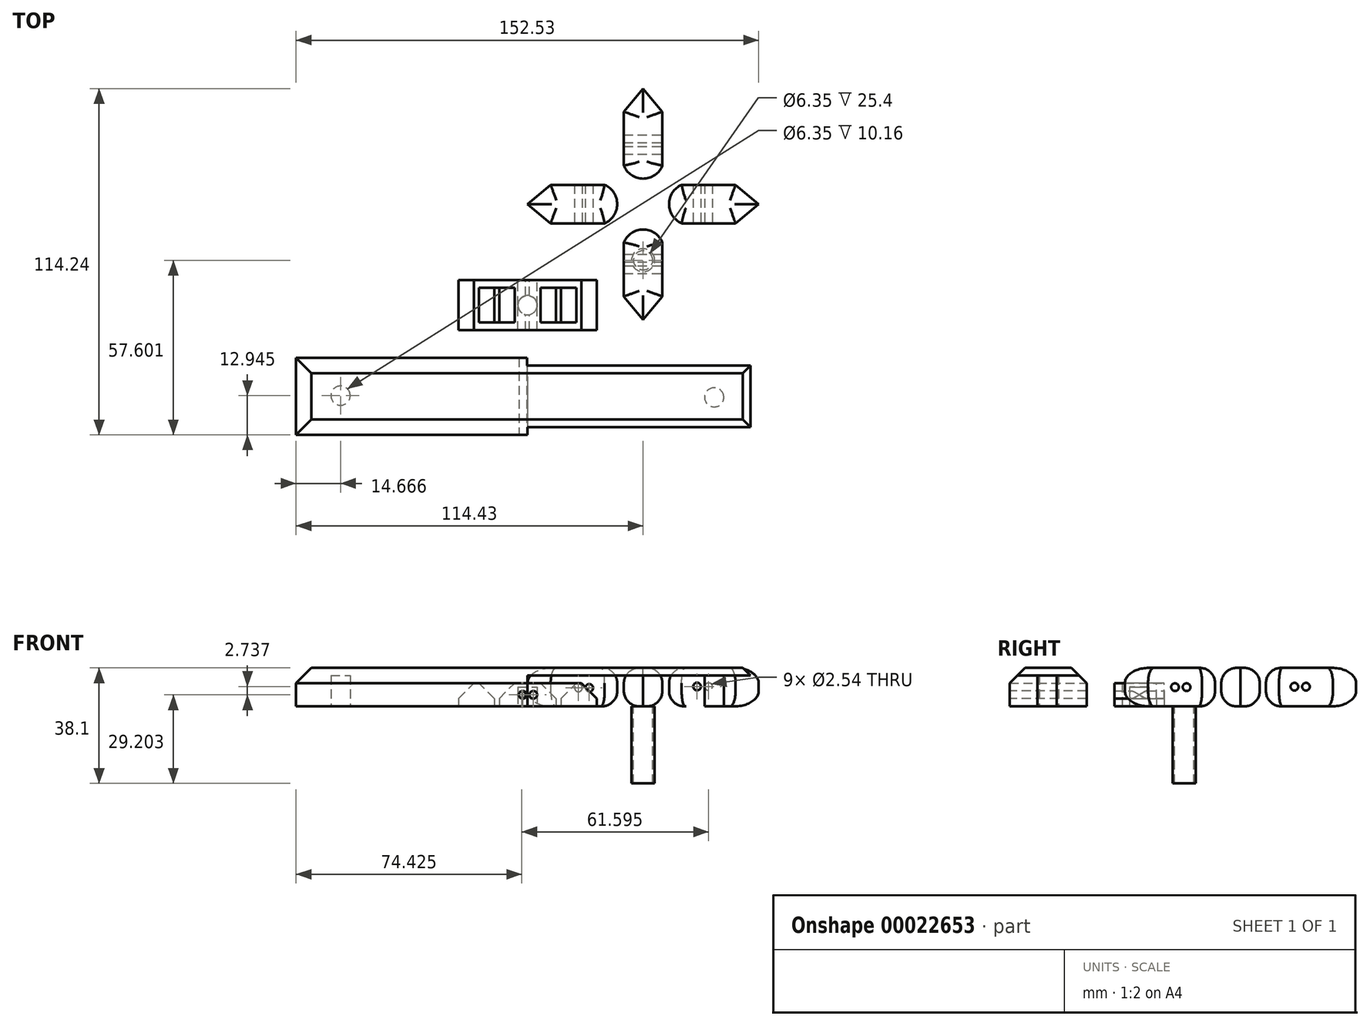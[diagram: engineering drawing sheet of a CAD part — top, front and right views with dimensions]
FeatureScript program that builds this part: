
annotation { "Feature Type Name" : "Feature", "Feature Type Description" : "" }
export const myFeature = defineFeature(function(context is Context, id is Id, definition is map)
    precondition{}
    {
        {
            var Q0;
            Q0=qCreatedBy(makeId("Top.planeOp"),FACE);
            var sketch = newSketch(context, id + "F0", { "sketchPlane" : qUnion([Q0])});
            skLineSegment(sketch, "E0.rect.bottom", {"start": v(76.2, 50.8) * mm, "end": v(-76.2, 50.8) * mm});
            skLineSegment(sketch, "E0.rect.top", {"start": v(76.2, -50.8) * mm, "end": v(-76.2, -50.8) * mm});
            skLineSegment(sketch, "E0.rect.left", {"start": v(76.2, 50.8) * mm, "end": v(76.2, -50.8) * mm});
            skLineSegment(sketch, "E0.rect.right", {"start": v(-76.2, 50.8) * mm, "end": v(-76.2, -50.8) * mm});
            skPoint(sketch, "E0.rect.middle", {"position": v(0, 0) * mm});
            skLineSegment(sketch, "E1", {"start": v(0, 0) * mm, "end": v(76.2, 0) * mm});
            skLineSegment(sketch, "E2", {"start": v(0, 0) * mm, "end": v(-76.2, 0) * mm});
            skLineSegment(sketch, "E3", {"start": v(-76.2, 0) * mm, "end": v(0, 0) * mm});
            skLineSegment(sketch, "E4", {"start": v(38.1, 0) * mm, "end": v(38.1, 12.7) * mm});
            skLineSegment(sketch, "E5", {"start": v(38.1, 0) * mm, "end": v(38.1, -12.7) * mm});
            skLineSegment(sketch, "E6", {"start": v(38.1, 12.7) * mm, "end": v(44.45, 12.7) * mm});
            skLineSegment(sketch, "E7", {"start": v(38.1, 12.7) * mm, "end": v(31.75, 12.7) * mm});
            skLineSegment(sketch, "E8.MirrorCS", {"start": v(38.1, -12.7) * mm, "end": v(44.45, -12.7) * mm});
            skLineSegment(sketch, "E9.MirrorCS", {"start": v(38.1, -12.7) * mm, "end": v(31.75, -12.7) * mm});
            skArc(sketch, "E10", {"start": v(31.75, 12.7) * mm, "mid": v(38.1, 8.38) * mm, "end": v(44.45, 12.7) * mm});
            skLineSegment(sketch, "E11.bottom", {"start": v(31.75, 12.7) * mm, "end": v(44.45, 12.7) * mm});
            skLineSegment(sketch, "E11.top", {"start": v(31.75, 30.48) * mm, "end": v(44.45, 30.48) * mm});
            skLineSegment(sketch, "E11.left", {"start": v(31.75, 12.7) * mm, "end": v(31.75, 30.48) * mm});
            skLineSegment(sketch, "E11.right", {"start": v(44.45, 12.7) * mm, "end": v(44.45, 30.48) * mm});
            skLineSegment(sketch, "E12", {"start": v(38.1, 12.7) * mm, "end": v(38.1, 38.1) * mm});
            skLineSegment(sketch, "E13", {"start": v(31.75, 30.48) * mm, "end": v(38.1, 38.1) * mm});
            skLineSegment(sketch, "E14", {"start": v(38.1, 38.1) * mm, "end": v(44.45, 30.48) * mm});
            skArc(sketch, "E15.MirrorCS", {"start": v(31.75, -12.7) * mm, "mid": v(38.1, -8.38) * mm, "end": v(44.45, -12.7) * mm});
            skLineSegment(sketch, "E16.MirrorCS", {"start": v(38.1, -12.7) * mm, "end": v(38.1, -38.1) * mm});
            skLineSegment(sketch, "E17.MirrorCS", {"start": v(44.45, -12.7) * mm, "end": v(44.45, -30.48) * mm});
            skLineSegment(sketch, "E18.MirrorCS", {"start": v(31.75, -12.7) * mm, "end": v(31.75, -30.48) * mm});
            skLineSegment(sketch, "E19.MirrorCS", {"start": v(31.75, -30.48) * mm, "end": v(44.45, -30.48) * mm});
            skLineSegment(sketch, "E20.MirrorCS", {"start": v(31.75, -30.48) * mm, "end": v(38.1, -38.1) * mm});
            skLineSegment(sketch, "E21.MirrorCS", {"start": v(38.1, -38.1) * mm, "end": v(44.45, -30.48) * mm});
            skLineSegment(sketch, "E22", {"start": v(25.4, 0) * mm, "end": v(25.4, 6.35) * mm});
            skLineSegment(sketch, "E23", {"start": v(25.4, 0) * mm, "end": v(25.4, -6.35) * mm});
            skLineSegment(sketch, "E24.bottom", {"start": v(25.4, 6.35) * mm, "end": v(7.62, 6.35) * mm});
            skLineSegment(sketch, "E24.top", {"start": v(25.4, -6.35) * mm, "end": v(7.62, -6.35) * mm});
            skLineSegment(sketch, "E24.left", {"start": v(25.4, 6.35) * mm, "end": v(25.4, -6.35) * mm});
            skLineSegment(sketch, "E24.right", {"start": v(7.62, 6.35) * mm, "end": v(7.62, -6.35) * mm});
            skLineSegment(sketch, "E25", {"start": v(25.4, 0) * mm, "end": v(0, 0) * mm});
            skLineSegment(sketch, "E26", {"start": v(7.62, 6.35) * mm, "end": v(0, 0) * mm});
            skLineSegment(sketch, "E27", {"start": v(0, 0) * mm, "end": v(7.62, -6.35) * mm});
            skArc(sketch, "E28", {"start": v(25.4, -6.35) * mm, "mid": v(29.56, 0) * mm, "end": v(25.4, 6.35) * mm});
            skLineSegment(sketch, "E29.MirrorCS", {"start": v(50.8, -6.35) * mm, "end": v(68.58, -6.35) * mm});
            skArc(sketch, "E30.MirrorCS", {"start": v(50.8, -6.35) * mm, "mid": v(46.64, 0) * mm, "end": v(50.8, 6.35) * mm});
            skLineSegment(sketch, "E31.MirrorCS", {"start": v(50.8, 6.35) * mm, "end": v(50.8, -6.35) * mm});
            skLineSegment(sketch, "E32.MirrorCS", {"start": v(50.8, 0) * mm, "end": v(76.2, 0) * mm});
            skLineSegment(sketch, "E33.MirrorCS", {"start": v(50.8, 6.35) * mm, "end": v(68.58, 6.35) * mm});
            skLineSegment(sketch, "E34.MirrorCS", {"start": v(68.58, 6.35) * mm, "end": v(68.58, -6.35) * mm});
            skLineSegment(sketch, "E35.MirrorCS", {"start": v(76.2, 0) * mm, "end": v(68.58, -6.35) * mm});
            skLineSegment(sketch, "E36.MirrorCS", {"start": v(68.58, 6.35) * mm, "end": v(76.2, 0) * mm});
            skLineSegment(sketch, "E37.left", {"start": v(-76.2, 27.95) * mm, "end": v(-76.2, 15.25) * mm});
            skLineSegment(sketch, "E38.left", {"start": v(-76.2, 12.7) * mm, "end": v(-76.2, 0) * mm});
            skLineSegment(sketch, "E39.left", {"start": v(-76.2, -3.5) * mm, "end": v(-76.2, -16.2) * mm});
            skLineSegment(sketch, "E40.left", {"start": v(-76.2, -18.75) * mm, "end": v(-76.2, -31.45) * mm});
            skLineSegment(sketch, "E41.rect.bottom", {"start": v(22.76, -25.12) * mm, "end": v(-22.76, -25.12) * mm});
            skLineSegment(sketch, "E41.rect.top", {"start": v(22.76, -41.6) * mm, "end": v(-22.76, -41.6) * mm});
            skLineSegment(sketch, "E41.rect.left", {"start": v(22.76, -25.12) * mm, "end": v(22.76, -41.6) * mm});
            skLineSegment(sketch, "E41.rect.right", {"start": v(-22.76, -25.12) * mm, "end": v(-22.76, -41.6) * mm});
            skPoint(sketch, "E41.rect.middle", {"position": v(0, -33.36) * mm});
            skLineSegment(sketch, "E42.rect.bottom", {"start": v(-9.34, -27.67) * mm, "end": v(-10.98, -27.67) * mm});
            skLineSegment(sketch, "E42.rect.top", {"start": v(-9.34, -39.06) * mm, "end": v(-10.98, -39.06) * mm});
            skLineSegment(sketch, "E42.rect.left", {"start": v(-9.34, -27.67) * mm, "end": v(-9.34, -39.06) * mm});
            skLineSegment(sketch, "E42.rect.right", {"start": v(-10.98, -27.67) * mm, "end": v(-10.98, -39.06) * mm});
            skPoint(sketch, "E42.rect.middle", {"position": v(-10.16, -33.36) * mm});
            skLineSegment(sketch, "E43.rect.bottom", {"start": v(9.3, -27.67) * mm, "end": v(11.01, -27.67) * mm});
            skLineSegment(sketch, "E43.rect.top", {"start": v(9.3, -39.06) * mm, "end": v(11.01, -39.06) * mm});
            skLineSegment(sketch, "E43.rect.left", {"start": v(9.3, -27.67) * mm, "end": v(9.3, -39.06) * mm});
            skLineSegment(sketch, "E43.rect.right", {"start": v(11.01, -27.67) * mm, "end": v(11.01, -39.06) * mm});
            skPoint(sketch, "E43.rect.middle", {"position": v(10.16, -33.36) * mm});
            skSolve(sketch);
        }
        {
            var Q0;
            {var subQ0=sQuery(id+"F0.wireOp",EDGE,"E28");var subQ1=sQuery(id+"F0.wireOp",EDGE,"E1");var subQ2=makeQuery(id+"F0.imprint","INTERSECT",VERTEX,{"derivedFrom":[subQ1,subQ0]});Q0=makeQuery(id+"F0.imprint","IMPRINT",FACE,{"disambiguationData":[TD([[makeQuery(id+"F0.imprint","IMPRINT",EDGE,{"disambiguationData":[TD([[subQ2,1.0]])],"derivedFrom":subQ1}),1.0]])]});}
            var Q1;
            {var subQ3=sQuery(id+"F0.wireOp",EDGE,"E29.MirrorCS");Q1=makeQuery(id+"F0.imprint","IMPRINT",FACE,{"disambiguationData":[TD([[makeQuery(id+"F0.imprint","IMPRINT",EDGE,{"derivedFrom":subQ3}),1.0]])]});}
            var Q2;
            {var subQ0=sQuery(id+"F0.wireOp",EDGE,"E36.MirrorCS");Q2=makeQuery(id+"F0.imprint","IMPRINT",FACE,{"disambiguationData":[TD([[makeQuery(id+"F0.imprint","IMPRINT",EDGE,{"derivedFrom":subQ0}),-1.0]])]});}
            var Q3;
            {var subQ3=sQuery(id+"F0.wireOp",EDGE,"E9.MirrorCS");Q3=makeQuery(id+"F0.imprint","IMPRINT",FACE,{"disambiguationData":[TD([[makeQuery(id+"F0.imprint","IMPRINT",EDGE,{"derivedFrom":subQ3}),-1.0]])]});}
            var Q4;
            {var subQ0=sQuery(id+"F0.wireOp",EDGE,"E35.MirrorCS");Q4=makeQuery(id+"F0.imprint","IMPRINT",FACE,{"disambiguationData":[TD([[makeQuery(id+"F0.imprint","IMPRINT",EDGE,{"derivedFrom":subQ0}),-1.0]])]});}
            var Q5;
            {var subQ1=sQuery(id+"F0.wireOp",EDGE,"E28");var subQ3=sQuery(id+"F0.wireOp",EDGE,"E1");var subQ5=makeQuery(id+"F0.imprint","INTERSECT",VERTEX,{"derivedFrom":[subQ3,subQ1]});Q5=makeQuery(id+"F0.imprint","IMPRINT",FACE,{"disambiguationData":[TD([[makeQuery(id+"F0.imprint","IMPRINT",EDGE,{"disambiguationData":[TD([[subQ5,1.0]])],"derivedFrom":subQ3}),-1.0]])]});}
            var Q6;
            {var subQ5=sQuery(id+"F0.wireOp",EDGE,"E24.bottom");Q6=makeQuery(id+"F0.imprint","IMPRINT",FACE,{"disambiguationData":[TD([[makeQuery(id+"F0.imprint","IMPRINT",EDGE,{"derivedFrom":subQ5}),1.0]])]});}
            var Q7;
            {var subQ0=sQuery(id+"F0.wireOp",EDGE,"E10");var subQ1=sQuery(id+"F0.wireOp",EDGE,"E4");var subQ2=makeQuery(id+"F0.imprint","INTERSECT",VERTEX,{"derivedFrom":[subQ1,subQ0]});Q7=makeQuery(id+"F0.imprint","IMPRINT",FACE,{"disambiguationData":[TD([[makeQuery(id+"F0.imprint","IMPRINT",EDGE,{"disambiguationData":[TD([[subQ2,-1.0]])],"derivedFrom":subQ1}),-1.0]])]});}
            var Q8;
            {var subQ5=sQuery(id+"F0.wireOp",EDGE,"E11.right");Q8=makeQuery(id+"F0.imprint","IMPRINT",FACE,{"disambiguationData":[TD([[makeQuery(id+"F0.imprint","IMPRINT",EDGE,{"derivedFrom":subQ5}),1.0]])]});}
            var Q9;
            {var subQ5=sQuery(id+"F0.wireOp",EDGE,"E24.top");Q9=makeQuery(id+"F0.imprint","IMPRINT",FACE,{"disambiguationData":[TD([[makeQuery(id+"F0.imprint","IMPRINT",EDGE,{"derivedFrom":subQ5}),-1.0]])]});}
            var Q10;
            {var subQ0=sQuery(id+"F0.wireOp",EDGE,"E21.MirrorCS");Q10=makeQuery(id+"F0.imprint","IMPRINT",FACE,{"disambiguationData":[TD([[makeQuery(id+"F0.imprint","IMPRINT",EDGE,{"derivedFrom":subQ0}),1.0]])]});}
            var Q11;
            {var subQ0=sQuery(id+"F0.wireOp",EDGE,"E27");Q11=makeQuery(id+"F0.imprint","IMPRINT",FACE,{"disambiguationData":[TD([[makeQuery(id+"F0.imprint","IMPRINT",EDGE,{"derivedFrom":subQ0}),1.0]])]});}
            var Q12;
            {var subQ1=sQuery(id+"F0.wireOp",EDGE,"E10");var subQ3=sQuery(id+"F0.wireOp",EDGE,"E4");var subQ5=makeQuery(id+"F0.imprint","INTERSECT",VERTEX,{"derivedFrom":[subQ3,subQ1]});Q12=makeQuery(id+"F0.imprint","IMPRINT",FACE,{"disambiguationData":[TD([[makeQuery(id+"F0.imprint","IMPRINT",EDGE,{"disambiguationData":[TD([[subQ5,-1.0]])],"derivedFrom":subQ3}),1.0]])]});}
            var Q13;
            {var subQ4=sQuery(id+"F0.wireOp",EDGE,"E8.MirrorCS");Q13=makeQuery(id+"F0.imprint","IMPRINT",FACE,{"disambiguationData":[TD([[makeQuery(id+"F0.imprint","IMPRINT",EDGE,{"derivedFrom":subQ4}),-1.0]])]});}
            var Q14;
            {var subQ3=sQuery(id+"F0.wireOp",EDGE,"E8.MirrorCS");Q14=makeQuery(id+"F0.imprint","IMPRINT",FACE,{"disambiguationData":[TD([[makeQuery(id+"F0.imprint","IMPRINT",EDGE,{"derivedFrom":subQ3}),1.0]])]});}
            var Q15;
            {var subQ1=sQuery(id+"F0.wireOp",EDGE,"E30.MirrorCS");var subQ3=sQuery(id+"F0.wireOp",EDGE,"E1");var subQ5=makeQuery(id+"F0.imprint","INTERSECT",VERTEX,{"derivedFrom":[subQ3,subQ1]});Q15=makeQuery(id+"F0.imprint","IMPRINT",FACE,{"disambiguationData":[TD([[makeQuery(id+"F0.imprint","IMPRINT",EDGE,{"disambiguationData":[TD([[subQ5,-1.0]])],"derivedFrom":subQ3}),1.0]])]});}
            var Q16;
            {var subQ0=sQuery(id+"F0.wireOp",EDGE,"E14");Q16=makeQuery(id+"F0.imprint","IMPRINT",FACE,{"disambiguationData":[TD([[makeQuery(id+"F0.imprint","IMPRINT",EDGE,{"derivedFrom":subQ0}),-1.0]])]});}
            var Q17;
            {var subQ1=sQuery(id+"F0.wireOp",EDGE,"E30.MirrorCS");var subQ3=sQuery(id+"F0.wireOp",EDGE,"E1");var subQ5=makeQuery(id+"F0.imprint","INTERSECT",VERTEX,{"derivedFrom":[subQ3,subQ1]});Q17=makeQuery(id+"F0.imprint","IMPRINT",FACE,{"disambiguationData":[TD([[makeQuery(id+"F0.imprint","IMPRINT",EDGE,{"disambiguationData":[TD([[subQ5,-1.0]])],"derivedFrom":subQ3}),-1.0]])]});}
            var Q18;
            {var subQ5=sQuery(id+"F0.wireOp",EDGE,"E11.left");Q18=makeQuery(id+"F0.imprint","IMPRINT",FACE,{"disambiguationData":[TD([[makeQuery(id+"F0.imprint","IMPRINT",EDGE,{"derivedFrom":subQ5}),-1.0]])]});}
            var Q19;
            {var subQ4=sQuery(id+"F0.wireOp",EDGE,"E9.MirrorCS");Q19=makeQuery(id+"F0.imprint","IMPRINT",FACE,{"disambiguationData":[TD([[makeQuery(id+"F0.imprint","IMPRINT",EDGE,{"derivedFrom":subQ4}),1.0]])]});}
            var Q20;
            {var subQ0=sQuery(id+"F0.wireOp",EDGE,"E20.MirrorCS");Q20=makeQuery(id+"F0.imprint","IMPRINT",FACE,{"disambiguationData":[TD([[makeQuery(id+"F0.imprint","IMPRINT",EDGE,{"derivedFrom":subQ0}),1.0]])]});}
            var Q21;
            {var subQ3=sQuery(id+"F0.wireOp",EDGE,"E33.MirrorCS");Q21=makeQuery(id+"F0.imprint","IMPRINT",FACE,{"disambiguationData":[TD([[makeQuery(id+"F0.imprint","IMPRINT",EDGE,{"derivedFrom":subQ3}),-1.0]])]});}
            var Q22;
            {var subQ0=sQuery(id+"F0.wireOp",EDGE,"E26");Q22=makeQuery(id+"F0.imprint","IMPRINT",FACE,{"disambiguationData":[TD([[makeQuery(id+"F0.imprint","IMPRINT",EDGE,{"derivedFrom":subQ0}),1.0]])]});}
            var Q23;
            {var subQ0=sQuery(id+"F0.wireOp",EDGE,"E13");Q23=makeQuery(id+"F0.imprint","IMPRINT",FACE,{"disambiguationData":[TD([[makeQuery(id+"F0.imprint","IMPRINT",EDGE,{"derivedFrom":subQ0}),-1.0]])]});}
            extrude(context, id + "F1", {"entities" : qUnion([Q0, Q1, Q2, Q3, Q4, Q5, Q6, Q7, Q8, Q9, Q10, Q11, Q12, Q13, Q14, Q15, Q16, Q17, Q18, Q19, Q20, Q21, Q22, Q23]), "depth" : 12.7 * mm});
        }
        {
            var Q0;
            Q0=makeQuery(id+"F1.opExtrude","CAP_FACE",FACE,{"disambiguationData":[OSD([sQuery(id+"F0.wireOp",EDGE,"E15.MirrorCS"),sQuery(id+"F0.wireOp",EDGE,"E17.MirrorCS"),sQuery(id+"F0.wireOp",EDGE,"E18.MirrorCS"),sQuery(id+"F0.wireOp",EDGE,"E20.MirrorCS"),sQuery(id+"F0.wireOp",EDGE,"E21.MirrorCS")])],"isStart":true});
            var sketch = newSketch(context, id + "F2", { "sketchPlane" : qUnion([Q0])});
            skCircle(sketch, "E44", {"center": v(38.1, 18.54) * mm, "radius": 3.18 * mm});
            skCircle(sketch, "E45", {"center": v(38.1, 18.54) * mm, "radius": 3.81 * mm});
            skLineSegment(sketch, "E46", {"start": v(0, 0) * mm, "end": v(108.17, 0) * mm});
            skLineSegment(sketch, "E47", {"start": v(38.1, 0) * mm, "end": v(38.1, -44.42) * mm});
            skLineSegment(sketch, "E48", {"start": v(38.1, 0) * mm, "end": v(38.1, 57.33) * mm});
            skCircle(sketch, "E49", {"center": v(19.4, 0) * mm, "radius": 3.18 * mm});
            skCircle(sketch, "E50", {"center": v(19.4, 0) * mm, "radius": 3.81 * mm});
            skCircle(sketch, "E51.MirrorC", {"center": v(38.1, -18.54) * mm, "radius": 3.81 * mm});
            skCircle(sketch, "E52.MirrorC", {"center": v(38.1, -18.54) * mm, "radius": 3.18 * mm});
            skCircle(sketch, "E53.MirrorC", {"center": v(56.8, 0) * mm, "radius": 3.81 * mm});
            skCircle(sketch, "E54.MirrorC", {"center": v(56.8, 0) * mm, "radius": 3.18 * mm});
            skCircle(sketch, "E55", {"center": v(0, 33.37) * mm, "radius": 3.18 * mm});
            skSolve(sketch);
        }
        {
            var Q0;
            {var subQ0=sQuery(id+"F2.wireOp",EDGE,"E48");var subQ3=sQuery(id+"F2.wireOp",EDGE,"E44");var subQ6=makeQuery(id+"F2.imprint","INTERSECT",VERTEX,{"disambiguationData":[OD(0.0)],"derivedFrom":[subQ3,subQ0]});Q0=makeQuery(id+"F2.imprint","IMPRINT",FACE,{"disambiguationData":[TD([[makeQuery(id+"F2.imprint","IMPRINT",EDGE,{"disambiguationData":[TD([[subQ6,1.0]])],"derivedFrom":subQ3}),-1.0]])]});}
            var Q1;
            {var subQ1=sQuery(id+"F2.wireOp",EDGE,"E47");var subQ4=sQuery(id+"F2.wireOp",EDGE,"E51.MirrorC");var subQ6=makeQuery(id+"F2.imprint","INTERSECT",VERTEX,{"disambiguationData":[OD(0.0)],"derivedFrom":[subQ1,subQ4]});Q1=makeQuery(id+"F2.imprint","IMPRINT",FACE,{"disambiguationData":[TD([[makeQuery(id+"F2.imprint","IMPRINT",EDGE,{"disambiguationData":[TD([[subQ6,-1.0]])],"derivedFrom":subQ1}),-1.0]])]});}
            var Q2;
            {var subQ0=sQuery(id+"F2.wireOp",EDGE,"E50");var subQ1=sQuery(id+"F2.wireOp",EDGE,"E46");var subQ3=makeQuery(id+"F2.imprint","INTERSECT",VERTEX,{"disambiguationData":[OD(0.0)],"derivedFrom":[subQ1,subQ0]});Q2=makeQuery(id+"F2.imprint","IMPRINT",FACE,{"disambiguationData":[TD([[makeQuery(id+"F2.imprint","IMPRINT",EDGE,{"disambiguationData":[TD([[subQ3,-1.0]])],"derivedFrom":subQ1}),1.0]])]});}
            var Q3;
            {var subQ1=sQuery(id+"F2.wireOp",EDGE,"E46");var subQ4=sQuery(id+"F2.wireOp",EDGE,"E53.MirrorC");var subQ6=makeQuery(id+"F2.imprint","INTERSECT",VERTEX,{"disambiguationData":[OD(0.0)],"derivedFrom":[subQ1,subQ4]});Q3=makeQuery(id+"F2.imprint","IMPRINT",FACE,{"disambiguationData":[TD([[makeQuery(id+"F2.imprint","IMPRINT",EDGE,{"disambiguationData":[TD([[subQ6,-1.0]])],"derivedFrom":subQ1}),1.0]])]});}
            var Q4;
            {var subQ1=sQuery(id+"F2.wireOp",EDGE,"E46");var subQ4=sQuery(id+"F2.wireOp",EDGE,"E53.MirrorC");var subQ6=makeQuery(id+"F2.imprint","INTERSECT",VERTEX,{"disambiguationData":[OD(0.0)],"derivedFrom":[subQ1,subQ4]});Q4=makeQuery(id+"F2.imprint","IMPRINT",FACE,{"disambiguationData":[TD([[makeQuery(id+"F2.imprint","IMPRINT",EDGE,{"disambiguationData":[TD([[subQ6,-1.0]])],"derivedFrom":subQ1}),-1.0]])]});}
            var Q5;
            {var subQ0=sQuery(id+"F2.wireOp",EDGE,"E48");var subQ3=sQuery(id+"F2.wireOp",EDGE,"E44");var subQ6=makeQuery(id+"F2.imprint","INTERSECT",VERTEX,{"disambiguationData":[OD(0.0)],"derivedFrom":[subQ3,subQ0]});Q5=makeQuery(id+"F2.imprint","IMPRINT",FACE,{"disambiguationData":[TD([[makeQuery(id+"F2.imprint","IMPRINT",EDGE,{"disambiguationData":[TD([[subQ6,-1.0]])],"derivedFrom":subQ3}),-1.0]])]});}
            var Q6;
            {var subQ1=sQuery(id+"F2.wireOp",EDGE,"E47");var subQ4=sQuery(id+"F2.wireOp",EDGE,"E51.MirrorC");var subQ6=makeQuery(id+"F2.imprint","INTERSECT",VERTEX,{"disambiguationData":[OD(0.0)],"derivedFrom":[subQ1,subQ4]});Q6=makeQuery(id+"F2.imprint","IMPRINT",FACE,{"disambiguationData":[TD([[makeQuery(id+"F2.imprint","IMPRINT",EDGE,{"disambiguationData":[TD([[subQ6,-1.0]])],"derivedFrom":subQ1}),1.0]])]});}
            var Q7;
            {var subQ0=sQuery(id+"F2.wireOp",EDGE,"E50");var subQ1=sQuery(id+"F2.wireOp",EDGE,"E46");var subQ3=makeQuery(id+"F2.imprint","INTERSECT",VERTEX,{"disambiguationData":[OD(0.0)],"derivedFrom":[subQ1,subQ0]});Q7=makeQuery(id+"F2.imprint","IMPRINT",FACE,{"disambiguationData":[TD([[makeQuery(id+"F2.imprint","IMPRINT",EDGE,{"disambiguationData":[TD([[subQ3,-1.0]])],"derivedFrom":subQ1}),-1.0]])]});}
            extrude(context, id + "F3", {"entities" : qUnion([Q0, Q1, Q2, Q3, Q4, Q5, Q6, Q7]), "depth" : 25.4 * mm});
        }
        {
            var Q0;
            Q0=makeQuery(id+"F1.opExtrude","SWEPT_FACE",FACE,{"disambiguationData":[OSD([sQuery(id+"F0.wireOp",EDGE,"E11.right")])]});
            var sketch = newSketch(context, id + "F4", { "sketchPlane" : qUnion([Q0])});
            skCircle(sketch, "E56", {"center": v(17.78, 6.47) * mm, "radius": 1.27 * mm});
            skCircle(sketch, "E57", {"center": v(21.6, 6.47) * mm, "radius": 1.27 * mm});
            skSolve(sketch);
        }
        {
            var Q0;
            Q0=makeQuery(id+"F4.imprint","IMPRINT",FACE,{"disambiguationData":[TD([[makeQuery(id+"F4.imprint","IMPRINT",EDGE,{"derivedFrom":sQuery(id+"F4.wireOp",EDGE,"E56")}),1.0]])]});
            var Q1;
            Q1=makeQuery(id+"F4.imprint","IMPRINT",FACE,{"disambiguationData":[TD([[makeQuery(id+"F4.imprint","IMPRINT",EDGE,{"derivedFrom":sQuery(id+"F4.wireOp",EDGE,"E57")}),1.0]])]});
            extrude(context, id + "F5", {"entities" : qUnion([Q0, Q1]), "operationType" : NewBodyOperationType.REMOVE, "oppositeDirection" : true, "depth" : 25.4 * mm});
        }
        {
            var Q0;
            Q0=makeQuery(id+"F1.opExtrude","SWEPT_FACE",FACE,{"disambiguationData":[OSD([sQuery(id+"F0.wireOp",EDGE,"E29.MirrorCS")])]});
            var sketch = newSketch(context, id + "F6", { "sketchPlane" : qUnion([Q0])});
            skCircle(sketch, "E58", {"center": v(55.88, 6.54) * mm, "radius": 1.27 * mm});
            skCircle(sketch, "E59", {"center": v(59.7, 6.54) * mm, "radius": 1.27 * mm});
            skSolve(sketch);
        }
        {
            var Q0;
            Q0=makeQuery(id+"F6.imprint","IMPRINT",FACE,{"disambiguationData":[TD([[makeQuery(id+"F6.imprint","IMPRINT",EDGE,{"derivedFrom":sQuery(id+"F6.wireOp",EDGE,"E58")}),1.0]])]});
            var Q1;
            Q1=makeQuery(id+"F6.imprint","IMPRINT",FACE,{"disambiguationData":[TD([[makeQuery(id+"F6.imprint","IMPRINT",EDGE,{"derivedFrom":sQuery(id+"F6.wireOp",EDGE,"E59")}),1.0]])]});
            extrude(context, id + "F7", {"entities" : qUnion([Q0, Q1]), "operationType" : NewBodyOperationType.REMOVE, "oppositeDirection" : true, "depth" : 25.4 * mm});
        }
        {
            var Q0;
            Q0=makeQuery(id+"F1.opExtrude","SWEPT_FACE",FACE,{"disambiguationData":[OSD([sQuery(id+"F0.wireOp",EDGE,"E17.MirrorCS")])]});
            var sketch = newSketch(context, id + "F8", { "sketchPlane" : qUnion([Q0])});
            skCircle(sketch, "E60", {"center": v(-17.78, 6.32) * mm, "radius": 1.27 * mm});
            skCircle(sketch, "E61", {"center": v(-21.59, 6.32) * mm, "radius": 1.27 * mm});
            skSolve(sketch);
        }
        {
            var Q0;
            Q0=makeQuery(id+"F8.imprint","IMPRINT",FACE,{"disambiguationData":[TD([[makeQuery(id+"F8.imprint","IMPRINT",EDGE,{"derivedFrom":sQuery(id+"F8.wireOp",EDGE,"E61")}),1.0]])]});
            var Q1;
            Q1=makeQuery(id+"F8.imprint","IMPRINT",FACE,{"disambiguationData":[TD([[makeQuery(id+"F8.imprint","IMPRINT",EDGE,{"derivedFrom":sQuery(id+"F8.wireOp",EDGE,"E60")}),1.0]])]});
            extrude(context, id + "F9", {"entities" : qUnion([Q0, Q1]), "operationType" : NewBodyOperationType.REMOVE, "oppositeDirection" : true, "depth" : 25.4 * mm});
        }
        {
            var Q0;
            Q0=makeQuery(id+"F1.opExtrude","SWEPT_FACE",FACE,{"disambiguationData":[OSD([sQuery(id+"F0.wireOp",EDGE,"E24.top")])]});
            var sketch = newSketch(context, id + "F10", { "sketchPlane" : qUnion([Q0])});
            skCircle(sketch, "E62", {"center": v(20.32, 6.09) * mm, "radius": 1.27 * mm});
            skCircle(sketch, "E63", {"center": v(16.76, 6.09) * mm, "radius": 1.27 * mm});
            skSolve(sketch);
        }
        {
            var Q0;
            Q0=makeQuery(id+"F10.imprint","IMPRINT",FACE,{"disambiguationData":[TD([[makeQuery(id+"F10.imprint","IMPRINT",EDGE,{"derivedFrom":sQuery(id+"F10.wireOp",EDGE,"E63")}),1.0]])]});
            var Q1;
            Q1=makeQuery(id+"F10.imprint","IMPRINT",FACE,{"disambiguationData":[TD([[makeQuery(id+"F10.imprint","IMPRINT",EDGE,{"derivedFrom":sQuery(id+"F10.wireOp",EDGE,"E62")}),1.0]])]});
            extrude(context, id + "F11", {"entities" : qUnion([Q0, Q1]), "operationType" : NewBodyOperationType.REMOVE, "oppositeDirection" : true, "depth" : 25.4 * mm});
        }
        {
            var Q0;
            Q0=makeQuery(id+"F1.opExtrude","CAP_FACE",FACE,{"disambiguationData":[OSD([sQuery(id+"F0.wireOp",EDGE,"E15.MirrorCS"),sQuery(id+"F0.wireOp",EDGE,"E17.MirrorCS"),sQuery(id+"F0.wireOp",EDGE,"E18.MirrorCS"),sQuery(id+"F0.wireOp",EDGE,"E20.MirrorCS"),sQuery(id+"F0.wireOp",EDGE,"E21.MirrorCS")])],"isStart":false});
            var Q1;
            Q1=makeQuery(id+"F1.opExtrude","CAP_FACE",FACE,{"disambiguationData":[OSD([sQuery(id+"F0.wireOp",EDGE,"E29.MirrorCS"),sQuery(id+"F0.wireOp",EDGE,"E30.MirrorCS"),sQuery(id+"F0.wireOp",EDGE,"E33.MirrorCS"),sQuery(id+"F0.wireOp",EDGE,"E35.MirrorCS"),sQuery(id+"F0.wireOp",EDGE,"E36.MirrorCS")])],"isStart":false});
            var Q2;
            Q2=makeQuery(id+"F1.opExtrude","CAP_FACE",FACE,{"disambiguationData":[OSD([sQuery(id+"F0.wireOp",EDGE,"E10"),sQuery(id+"F0.wireOp",EDGE,"E11.left"),sQuery(id+"F0.wireOp",EDGE,"E11.right"),sQuery(id+"F0.wireOp",EDGE,"E13"),sQuery(id+"F0.wireOp",EDGE,"E14")])],"isStart":false});
            var Q3;
            Q3=makeQuery(id+"F1.opExtrude","CAP_FACE",FACE,{"disambiguationData":[OSD([sQuery(id+"F0.wireOp",EDGE,"E24.bottom"),sQuery(id+"F0.wireOp",EDGE,"E24.top"),sQuery(id+"F0.wireOp",EDGE,"E26"),sQuery(id+"F0.wireOp",EDGE,"E27"),sQuery(id+"F0.wireOp",EDGE,"E28")])],"isStart":false});
            fillet(context, id + "F12", {"entities" : qUnion([Q0, Q1, Q2, Q3]), "radius" : 5.08 * mm, "tangentPropagation" : true, "allowEdgeOverflow" : false});
        }
        {
            var Q0;
            Q0=makeQuery(id+"F1.opExtrude","CAP_FACE",FACE,{"disambiguationData":[OSD([sQuery(id+"F0.wireOp",EDGE,"E15.MirrorCS"),sQuery(id+"F0.wireOp",EDGE,"E17.MirrorCS"),sQuery(id+"F0.wireOp",EDGE,"E18.MirrorCS"),sQuery(id+"F0.wireOp",EDGE,"E20.MirrorCS"),sQuery(id+"F0.wireOp",EDGE,"E21.MirrorCS")])],"isStart":true});
            var Q1;
            Q1=makeQuery(id+"F1.opExtrude","CAP_FACE",FACE,{"disambiguationData":[OSD([sQuery(id+"F0.wireOp",EDGE,"E29.MirrorCS"),sQuery(id+"F0.wireOp",EDGE,"E30.MirrorCS"),sQuery(id+"F0.wireOp",EDGE,"E33.MirrorCS"),sQuery(id+"F0.wireOp",EDGE,"E35.MirrorCS"),sQuery(id+"F0.wireOp",EDGE,"E36.MirrorCS")])],"isStart":true});
            var Q2;
            Q2=makeQuery(id+"F1.opExtrude","CAP_FACE",FACE,{"disambiguationData":[OSD([sQuery(id+"F0.wireOp",EDGE,"E24.bottom"),sQuery(id+"F0.wireOp",EDGE,"E24.top"),sQuery(id+"F0.wireOp",EDGE,"E26"),sQuery(id+"F0.wireOp",EDGE,"E27"),sQuery(id+"F0.wireOp",EDGE,"E28")])],"isStart":true});
            var Q3;
            Q3=makeQuery(id+"F1.opExtrude","CAP_FACE",FACE,{"disambiguationData":[OSD([sQuery(id+"F0.wireOp",EDGE,"E10"),sQuery(id+"F0.wireOp",EDGE,"E11.left"),sQuery(id+"F0.wireOp",EDGE,"E11.right"),sQuery(id+"F0.wireOp",EDGE,"E13"),sQuery(id+"F0.wireOp",EDGE,"E14")])],"isStart":true});
            fillet(context, id + "F13", {"entities" : qUnion([Q0, Q1, Q2, Q3]), "radius" : 5.08 * mm, "tangentPropagation" : true, "allowEdgeOverflow" : false});
        }
        {
            var Q0;
            Q0=qCreatedBy(makeId("Top.planeOp"),FACE);
            var sketch = newSketch(context, id + "F14", { "sketchPlane" : qUnion([Q0])});
            skLineSegment(sketch, "E64.bottom", {"start": v(-76.33, -50.74) * mm, "end": v(76.07, -50.74) * mm});
            skLineSegment(sketch, "E64.top", {"start": v(-76.33, -76.14) * mm, "end": v(76.07, -76.14) * mm});
            skLineSegment(sketch, "E64.left", {"start": v(-76.33, -50.74) * mm, "end": v(-76.33, -76.14) * mm});
            skLineSegment(sketch, "E64.right", {"start": v(76.07, -50.74) * mm, "end": v(76.07, -76.14) * mm});
            skSolve(sketch);
        }
        {
            var Q0;
            Q0=makeQuery(id+"F14.imprint","IMPRINT",FACE,{"disambiguationData":[TD([[makeQuery(id+"F14.imprint","IMPRINT",EDGE,{"derivedFrom":sQuery(id+"F14.wireOp",EDGE,"E64.bottom")}),-1.0]])]});
            extrude(context, id + "F15", {"entities" : qUnion([Q0]), "depth" : 12.7 * mm});
        }
        {
            var Q0;
            Q0=makeQuery(id+"F15.opExtrude","CAP_FACE",FACE,{"disambiguationData":[OSD([sQuery(id+"F14.wireOp",EDGE,"E64.bottom"),sQuery(id+"F14.wireOp",EDGE,"E64.top"),sQuery(id+"F14.wireOp",EDGE,"E64.left"),sQuery(id+"F14.wireOp",EDGE,"E64.right")])],"isStart":false});
            chamfer(context, id + "F16", {"entities" : qUnion([Q0]), "width" : 5.08 * mm, "tangentPropagation" : true});
        }
        {
            var Q0;
            Q0=makeQuery(id+"F15.opExtrude","SWEPT_FACE",FACE,{"disambiguationData":[OSD([sQuery(id+"F14.wireOp",EDGE,"E64.top")])]});
            var sketch = newSketch(context, id + "F17", { "sketchPlane" : qUnion([Q0])});
            skCircle(sketch, "E65", {"center": v(-1.56, 3.8) * mm, "radius": 1.27 * mm});
            skCircle(sketch, "E66", {"center": v(2, 3.8) * mm, "radius": 1.27 * mm});
            skSolve(sketch);
        }
        {
            var Q0;
            Q0=makeQuery(id+"F17.imprint","IMPRINT",FACE,{"disambiguationData":[TD([[makeQuery(id+"F17.imprint","IMPRINT",EDGE,{"derivedFrom":sQuery(id+"F17.wireOp",EDGE,"E65")}),1.0]])]});
            var Q1;
            Q1=makeQuery(id+"F17.imprint","IMPRINT",FACE,{"disambiguationData":[TD([[makeQuery(id+"F17.imprint","IMPRINT",EDGE,{"derivedFrom":sQuery(id+"F17.wireOp",EDGE,"E66")}),1.0]])]});
            extrude(context, id + "F18", {"entities" : qUnion([Q0, Q1]), "operationType" : NewBodyOperationType.REMOVE, "oppositeDirection" : true, "depth" : 50.8 * mm});
        }
        {
            var Q0;
            Q0=makeQuery(id+"F15.opExtrude","CAP_FACE",FACE,{"disambiguationData":[OSD([sQuery(id+"F14.wireOp",EDGE,"E64.bottom"),sQuery(id+"F14.wireOp",EDGE,"E64.top"),sQuery(id+"F14.wireOp",EDGE,"E64.left"),sQuery(id+"F14.wireOp",EDGE,"E64.right")])],"isStart":true});
            var sketch = newSketch(context, id + "F19", { "sketchPlane" : qUnion([Q0])});
            skCircle(sketch, "E67", {"center": v(-61.66, 63.2) * mm, "radius": 3.18 * mm});
            skLineSegment(sketch, "E68", {"start": v(-76.33, 63.44) * mm, "end": v(76.07, 63.2) * mm});
            skCircle(sketch, "E69", {"center": v(61.53, 63.75) * mm, "radius": 3.18 * mm});
            skLineSegment(sketch, "E70", {"start": v(-0.13, 50.74) * mm, "end": v(0, 76.14) * mm});
            skSolve(sketch);
        }
        {
            var Q0;
            {var subQ0=sQuery(id+"F19.wireOp",EDGE,"E68");var subQ1=sQuery(id+"F19.wireOp",EDGE,"E67");var subQ3=makeQuery(id+"F19.imprint","INTERSECT",VERTEX,{"disambiguationData":[OD(0.0)],"derivedFrom":[subQ1,subQ0]});Q0=makeQuery(id+"F19.imprint","IMPRINT",FACE,{"disambiguationData":[TD([[makeQuery(id+"F19.imprint","IMPRINT",EDGE,{"disambiguationData":[TD([[subQ3,-1.0]])],"derivedFrom":subQ1}),1.0]])]});}
            var Q1;
            {var subQ0=sQuery(id+"F19.wireOp",EDGE,"E69");var subQ1=sQuery(id+"F19.wireOp",EDGE,"E68");var subQ3=makeQuery(id+"F19.imprint","INTERSECT",VERTEX,{"disambiguationData":[OD(0.0)],"derivedFrom":[subQ1,subQ0]});Q1=makeQuery(id+"F19.imprint","IMPRINT",FACE,{"disambiguationData":[TD([[makeQuery(id+"F19.imprint","IMPRINT",EDGE,{"disambiguationData":[TD([[subQ3,-1.0]])],"derivedFrom":subQ1}),1.0]])]});}
            var Q2;
            {var subQ0=sQuery(id+"F19.wireOp",EDGE,"E69");var subQ1=sQuery(id+"F19.wireOp",EDGE,"E68");var subQ3=makeQuery(id+"F19.imprint","INTERSECT",VERTEX,{"disambiguationData":[OD(0.0)],"derivedFrom":[subQ1,subQ0]});Q2=makeQuery(id+"F19.imprint","IMPRINT",FACE,{"disambiguationData":[TD([[makeQuery(id+"F19.imprint","IMPRINT",EDGE,{"disambiguationData":[TD([[subQ3,-1.0]])],"derivedFrom":subQ1}),-1.0]])]});}
            var Q3;
            {var subQ0=sQuery(id+"F19.wireOp",EDGE,"E68");var subQ1=sQuery(id+"F19.wireOp",EDGE,"E67");var subQ3=makeQuery(id+"F19.imprint","INTERSECT",VERTEX,{"disambiguationData":[OD(0.0)],"derivedFrom":[subQ1,subQ0]});Q3=makeQuery(id+"F19.imprint","IMPRINT",FACE,{"disambiguationData":[TD([[makeQuery(id+"F19.imprint","IMPRINT",EDGE,{"disambiguationData":[TD([[subQ3,1.0]])],"derivedFrom":subQ1}),1.0]])]});}
            extrude(context, id + "F20", {"entities" : qUnion([Q0, Q1, Q2, Q3]), "operationType" : NewBodyOperationType.REMOVE, "oppositeDirection" : true, "depth" : 10.16 * mm});
        }
        {
            var Q0;
            Q0=makeQuery(id+"F0.imprint","IMPRINT",FACE,{"disambiguationData":[TD([[makeQuery(id+"F0.imprint","IMPRINT",EDGE,{"derivedFrom":sQuery(id+"F0.wireOp",EDGE,"E41.rect.bottom")}),1.0]])]});
            extrude(context, id + "F21", {"entities" : qUnion([Q0]), "depth" : 7.62 * mm});
        }
        {
            var Q0;
            Q0=makeQuery(id+"F2.imprint","IMPRINT",FACE,{"disambiguationData":[TD([[makeQuery(id+"F2.imprint","IMPRINT",EDGE,{"derivedFrom":sQuery(id+"F2.wireOp",EDGE,"E55")}),1.0]])]});
            extrude(context, id + "F22", {"entities" : qUnion([Q0]), "operationType" : NewBodyOperationType.REMOVE, "oppositeDirection" : true, "depth" : 6.35 * mm});
        }
        {
            var Q0;
            Q0=makeQuery(id+"F21.opExtrude","SWEPT_FACE",FACE,{"disambiguationData":[OSD([sQuery(id+"F0.wireOp",EDGE,"E41.rect.bottom")])]});
            var sketch = newSketch(context, id + "F23", { "sketchPlane" : qUnion([Q0])});
            skLineSegment(sketch, "E71", {"start": v(0, 7.62) * mm, "end": v(0, 0) * mm, "construction": true});
            skCircle(sketch, "E72", {"center": v(1.9, 3.8) * mm, "radius": 1.27 * mm});
            skPoint(sketch, "E72.centerSnap0", {"position": v(0, 3.81) * mm});
            skCircle(sketch, "E73", {"center": v(-1.9, 3.8) * mm, "radius": 1.27 * mm});
            skSolve(sketch);
        }
        {
            var Q0;
            Q0=makeQuery(id+"F23.imprint","IMPRINT",FACE,{"disambiguationData":[TD([[makeQuery(id+"F23.imprint","IMPRINT",EDGE,{"derivedFrom":sQuery(id+"F23.wireOp",EDGE,"E72")}),1.0]])]});
            var Q1;
            Q1=makeQuery(id+"F23.imprint","IMPRINT",FACE,{"disambiguationData":[TD([[makeQuery(id+"F23.imprint","IMPRINT",EDGE,{"derivedFrom":sQuery(id+"F23.wireOp",EDGE,"E73")}),1.0]])]});
            extrude(context, id + "F24", {"entities" : qUnion([Q0, Q1]), "operationType" : NewBodyOperationType.REMOVE, "oppositeDirection" : true, "depth" : 25.4 * mm});
        }
        {
            var Q0;
            Q0=makeQuery(id+"F21.opExtrude","CAP_EDGE",EDGE,{"disambiguationData":[OSD([sQuery(id+"F0.wireOp",EDGE,"E42.rect.left")])],"isStart":false});
            var Q1;
            Q1=makeQuery(id+"F21.opExtrude","CAP_EDGE",EDGE,{"disambiguationData":[OSD([sQuery(id+"F0.wireOp",EDGE,"E43.rect.left")])],"isStart":false});
            var Q2;
            Q2=makeQuery(id+"F21.opExtrude","CAP_EDGE",EDGE,{"disambiguationData":[OSD([sQuery(id+"F0.wireOp",EDGE,"E43.rect.right")])],"isStart":false});
            var Q3;
            Q3=makeQuery(id+"F21.opExtrude","CAP_EDGE",EDGE,{"disambiguationData":[OSD([sQuery(id+"F0.wireOp",EDGE,"E42.rect.right")])],"isStart":false});
            var Q4;
            Q4=makeQuery(id+"F21.opExtrude","CAP_EDGE",EDGE,{"disambiguationData":[OSD([sQuery(id+"F0.wireOp",EDGE,"E41.rect.left")])],"isStart":false});
            var Q5;
            Q5=makeQuery(id+"F21.opExtrude","CAP_EDGE",EDGE,{"disambiguationData":[OSD([sQuery(id+"F0.wireOp",EDGE,"E41.rect.right")])],"isStart":false});
            chamfer(context, id + "F25", {"entities" : qUnion([Q0, Q1, Q2, Q3, Q4, Q5]), "width" : 5.08 * mm, "tangentPropagation" : true});
        }
    });
